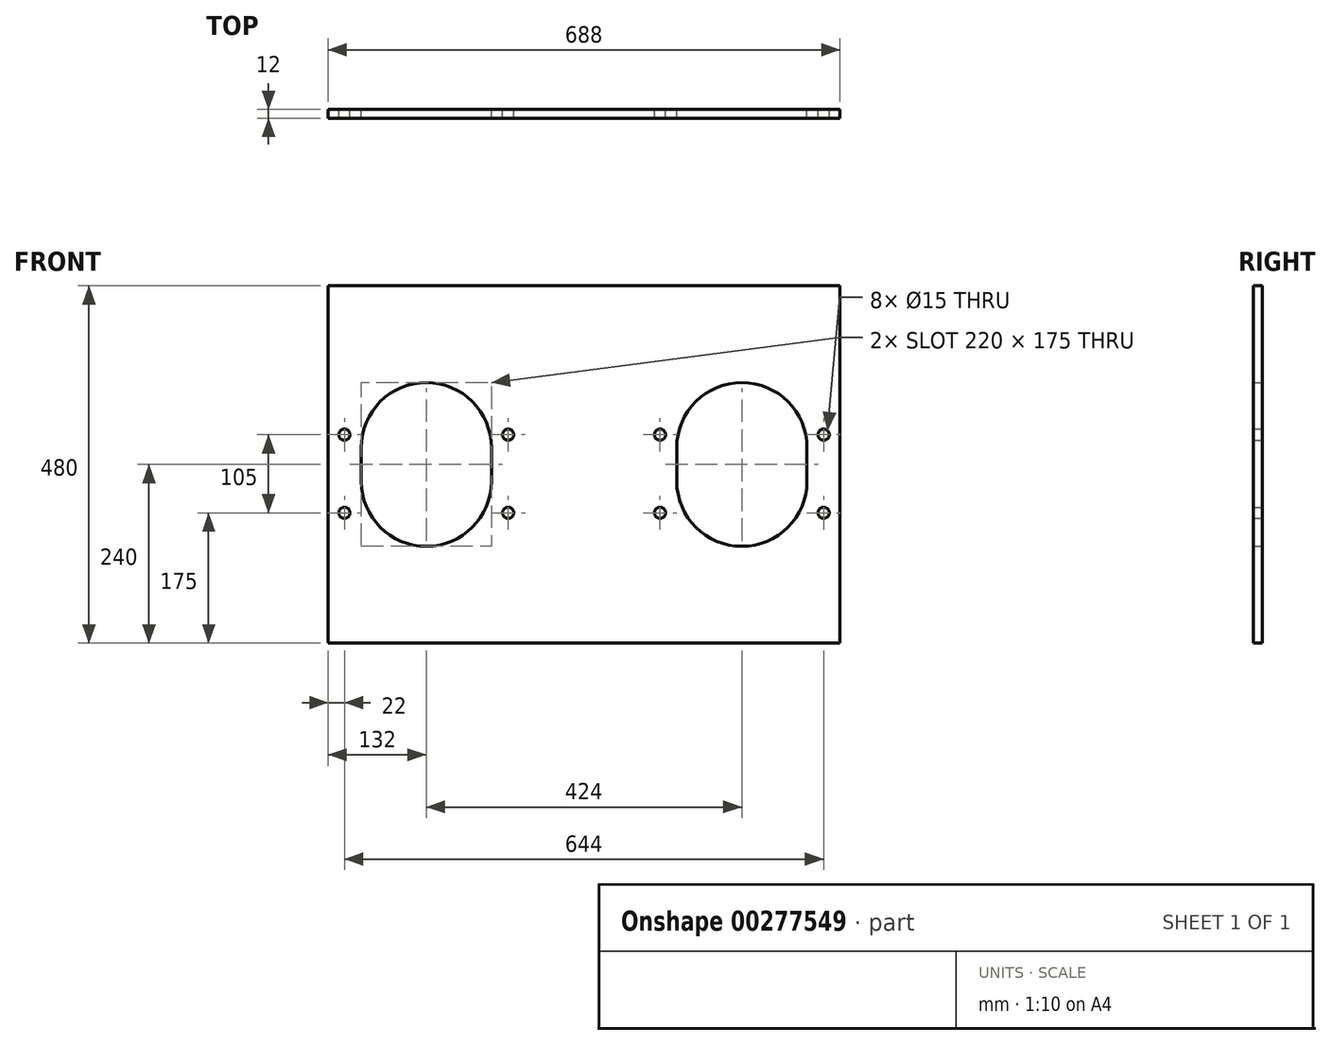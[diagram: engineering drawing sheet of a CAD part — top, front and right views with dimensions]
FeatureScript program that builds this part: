
annotation { "Feature Type Name" : "Feature", "Feature Type Description" : "" }
export const myFeature = defineFeature(function(context is Context, id is Id, definition is map)
    precondition{}
    {
        {
            var Q0;
            Q0=qCreatedBy(makeId("Front.planeOp"),FACE);
            var sketch = newSketch(context, id + "F0", { "sketchPlane" : qUnion([Q0])});
            skLineSegment(sketch, "E0.bottom", {"start": v(0, 0) * mm, "end": v(688, 0) * mm});
            skLineSegment(sketch, "E0.top", {"start": v(0, 300) * mm, "end": v(688, 300) * mm});
            skLineSegment(sketch, "E0.left", {"start": v(0, 0) * mm, "end": v(0, 300) * mm});
            skLineSegment(sketch, "E0.right", {"start": v(688, 0) * mm, "end": v(688, 300) * mm});
            skCircle(sketch, "E1", {"center": v(22, 190) * mm, "radius": 7.5 * mm});
            skCircle(sketch, "E2", {"center": v(22, 85) * mm, "radius": 7.5 * mm});
            skCircle(sketch, "E3", {"center": v(242, 190) * mm, "radius": 7.5 * mm});
            skCircle(sketch, "E4", {"center": v(242, 85) * mm, "radius": 7.5 * mm});
            skCircle(sketch, "E5", {"center": v(666, 190) * mm, "radius": 7.5 * mm});
            skCircle(sketch, "E6", {"center": v(666, 85) * mm, "radius": 7.5 * mm});
            skCircle(sketch, "E7", {"center": v(446, 190) * mm, "radius": 7.5 * mm});
            skCircle(sketch, "E8", {"center": v(446, 85) * mm, "radius": 7.5 * mm});
            skCircle(sketch, "E9", {"center": v(556, 172.5) * mm, "radius": 87.5 * mm});
            skCircle(sketch, "E10", {"center": v(556, 127.5) * mm, "radius": 87.5 * mm});
            skCircle(sketch, "E11", {"center": v(132, 172.5) * mm, "radius": 87.5 * mm});
            skCircle(sketch, "E12", {"center": v(132, 127.5) * mm, "radius": 87.5 * mm});
            skLineSegment(sketch, "E13", {"start": v(44.5, 172.5) * mm, "end": v(44.5, 127.5) * mm});
            skLineSegment(sketch, "E14", {"start": v(219.5, 172.5) * mm, "end": v(219.5, 127.5) * mm});
            skLineSegment(sketch, "E15", {"start": v(468.5, 172.5) * mm, "end": v(468.5, 127.5) * mm});
            skLineSegment(sketch, "E16", {"start": v(643.5, 172.5) * mm, "end": v(643.5, 127.5) * mm});
            skLineSegment(sketch, "E17.top", {"start": v(0, 390) * mm, "end": v(688, 390) * mm});
            skLineSegment(sketch, "E17.left", {"start": v(0, 300) * mm, "end": v(0, 390) * mm});
            skLineSegment(sketch, "E17.right", {"start": v(688, 300) * mm, "end": v(688, 390) * mm});
            skLineSegment(sketch, "E18.top", {"start": v(0, -90) * mm, "end": v(688, -90) * mm});
            skLineSegment(sketch, "E18.left", {"start": v(0, 0) * mm, "end": v(0, -90) * mm});
            skLineSegment(sketch, "E18.right", {"start": v(688, 0) * mm, "end": v(688, -90) * mm});
            skSolve(sketch);
        }
        {
            var Q0;
            Q0=makeQuery(id+"F0.imprint","IMPRINT",FACE,{"disambiguationData":[TD([[makeQuery(id+"F0.imprint","IMPRINT",EDGE,{"derivedFrom":sQuery(id+"F0.wireOp",EDGE,"E0.top")}),1.0]])]});
            var Q1;
            Q1=makeQuery(id+"F0.imprint","IMPRINT",FACE,{"disambiguationData":[TD([[makeQuery(id+"F0.imprint","IMPRINT",EDGE,{"derivedFrom":sQuery(id+"F0.wireOp",EDGE,"E0.left")}),-1.0]])]});
            var Q2;
            Q2=makeQuery(id+"F0.imprint","IMPRINT",FACE,{"disambiguationData":[TD([[makeQuery(id+"F0.imprint","IMPRINT",EDGE,{"derivedFrom":sQuery(id+"F0.wireOp",EDGE,"E0.bottom")}),-1.0]])]});
            extrude(context, id + "F1", {"entities" : qUnion([Q0, Q1, Q2]), "flatOperationType" : FlatOperationType.REMOVE, "offsetDistance" : 25 * mm, "depth" : 12 * mm, "domain" : OperationDomain.MODEL});
        }
    });
